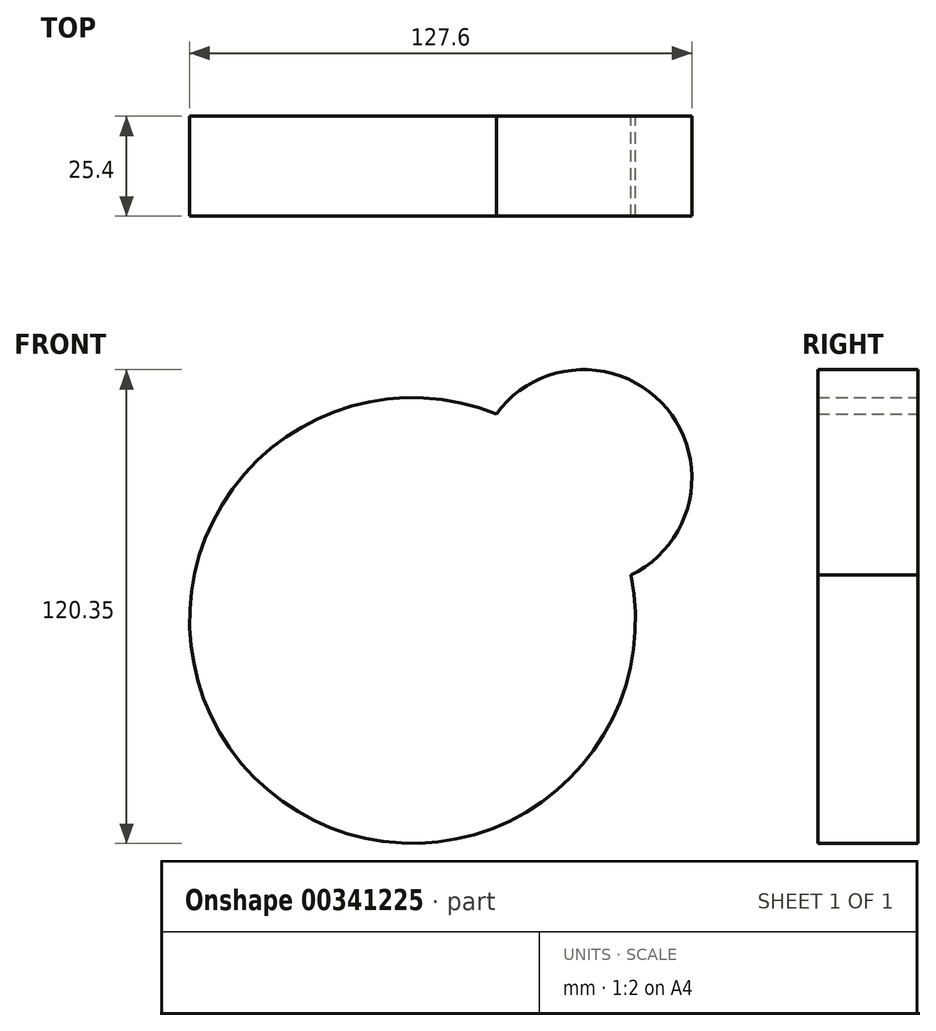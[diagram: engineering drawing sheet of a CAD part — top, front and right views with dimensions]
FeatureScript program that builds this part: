
annotation { "Feature Type Name" : "Feature", "Feature Type Description" : "" }
export const myFeature = defineFeature(function(context is Context, id is Id, definition is map)
    precondition{}
    {
        {
            var Q0;
            Q0=qCreatedBy(makeId("Front.planeOp"),FACE);
            var sketch = newSketch(context, id + "F0", { "sketchPlane" : qUnion([Q0])});
            skCircle(sketch, "E0", {"center": v(0, 0) * mm, "radius": 56.62 * mm});
            skCircle(sketch, "E1", {"center": v(43.5, 36.25) * mm, "radius": 27.48 * mm});
            skSolve(sketch);
        }
        {
            var Q0;
            Q0 = qSketchRegion(id + "F0", true);
            extrude(context, id + "F1", {"entities" : qUnion([Q0]), "depth" : 25.4 * mm});
        }
    });
